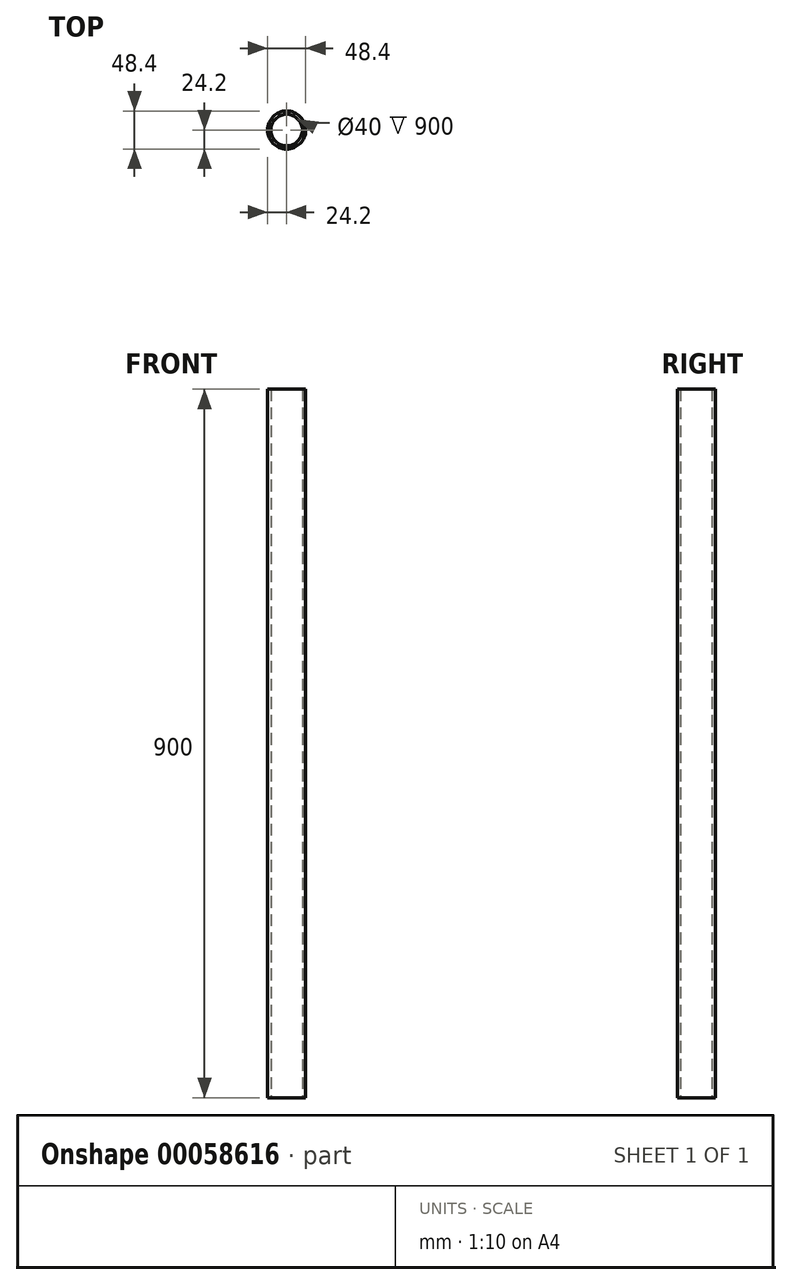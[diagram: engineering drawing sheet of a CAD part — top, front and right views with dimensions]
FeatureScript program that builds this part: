
annotation { "Feature Type Name" : "Feature", "Feature Type Description" : "" }
export const myFeature = defineFeature(function(context is Context, id is Id, definition is map)
    precondition{}
    {
        {
            var Q0;
            Q0=qCreatedBy(makeId("Top.planeOp"),FACE);
            var sketch = newSketch(context, id + "F0", { "sketchPlane" : qUnion([Q0])});
            skCircle(sketch, "E0", {"center": v(0, 0) * mm, "radius": 24.2 * mm});
            skCircle(sketch, "E1", {"center": v(0, 0) * mm, "radius": 20 * mm});
            skSolve(sketch);
        }
        {
            var Q0;
            Q0 = qSketchRegion(id + "F0", true);
            extrude(context, id + "F1", {"entities" : qUnion([Q0]), "depth" : 900 * mm});
        }
    });
